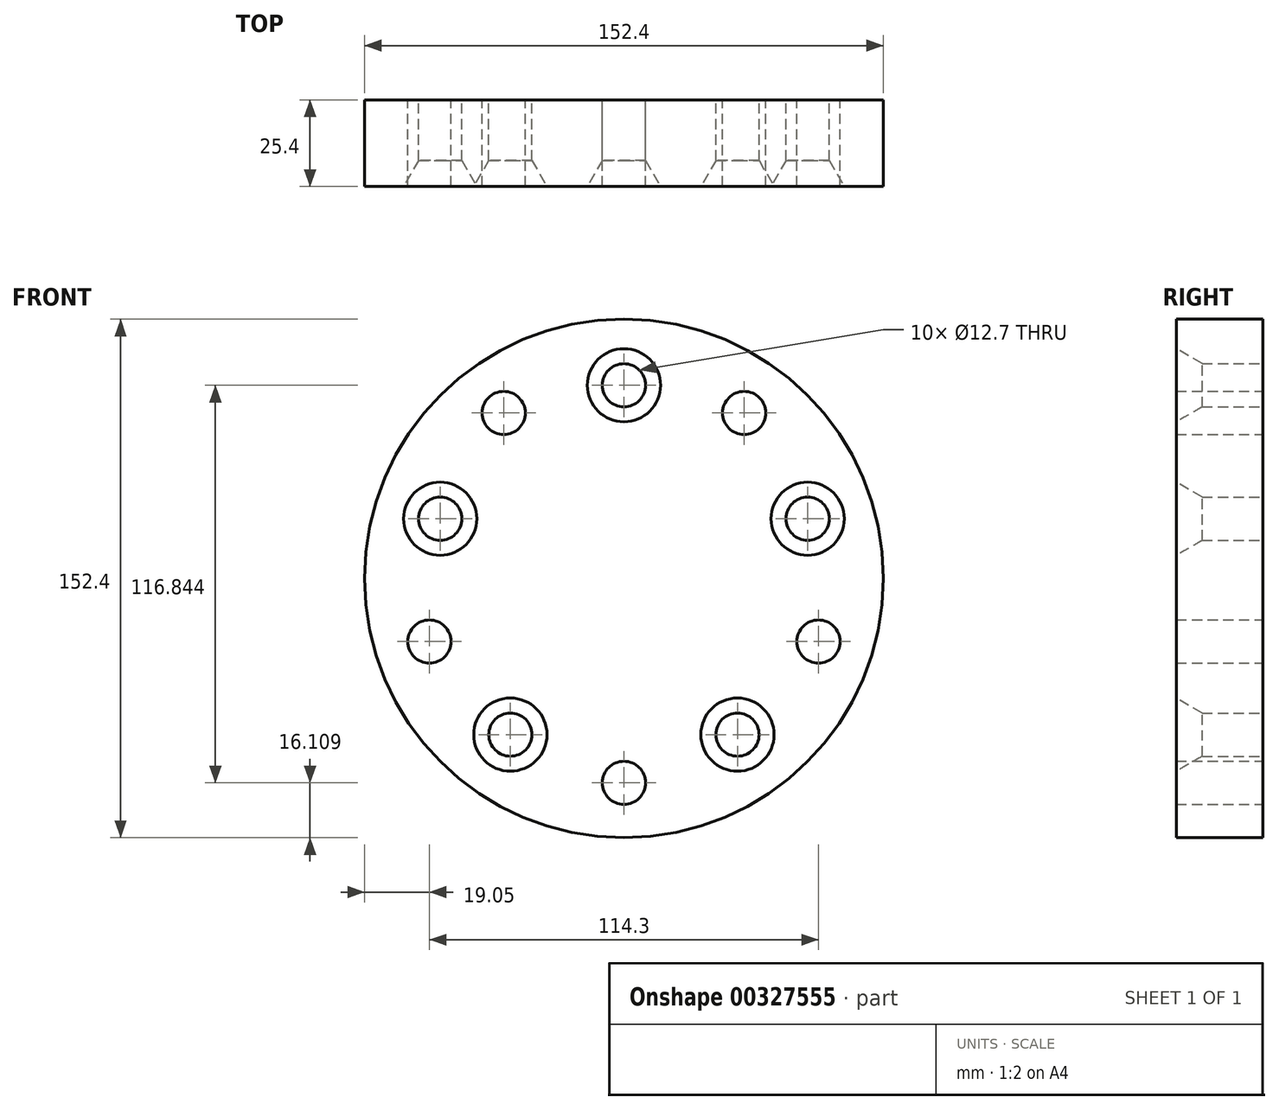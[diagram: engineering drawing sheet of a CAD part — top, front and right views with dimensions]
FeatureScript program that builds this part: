
annotation { "Feature Type Name" : "Feature", "Feature Type Description" : "" }
export const myFeature = defineFeature(function(context is Context, id is Id, definition is map)
    precondition{}
    {
        {
            var Q0;
            Q0=qCreatedBy(makeId("Front.planeOp"),FACE);
            var sketch = newSketch(context, id + "F0", { "sketchPlane" : qUnion([Q0])});
            skCircle(sketch, "E0", {"center": v(0, 0) * mm, "radius": 76.2 * mm});
            skCircle(sketch, "E1", {"center": v(0, 56.75) * mm, "radius": 6.35 * mm});
            skCircle(sketch, "E2.1.0", {"center": v(-53.97, 17.54) * mm, "radius": 6.35 * mm});
            skCircle(sketch, "E2.2.0", {"center": v(-33.36, -45.91) * mm, "radius": 6.35 * mm});
            skCircle(sketch, "E2.3.0", {"center": v(33.36, -45.91) * mm, "radius": 6.35 * mm});
            skCircle(sketch, "E2.4.0", {"center": v(53.98, 17.54) * mm, "radius": 6.35 * mm});
            skCircle(sketch, "E3", {"center": v(0, -60.1) * mm, "radius": 6.35 * mm});
            skCircle(sketch, "E4.1.0", {"center": v(57.15, -18.57) * mm, "radius": 6.35 * mm});
            skCircle(sketch, "E4.2.0", {"center": v(35.32, 48.61) * mm, "radius": 6.35 * mm});
            skCircle(sketch, "E4.3.0", {"center": v(-35.32, 48.61) * mm, "radius": 6.35 * mm});
            skCircle(sketch, "E4.4.0", {"center": v(-57.15, -18.57) * mm, "radius": 6.35 * mm});
            skSolve(sketch);
        }
        {
            var Q0;
            Q0 = qSketchRegion(id + "F0", true);
            extrude(context, id + "F1", {"entities" : qUnion([Q0]), "depth" : 25.4 * mm});
        }
        {
            var Q0;
            Q0=makeQuery(id+"F1.opExtrude","CAP_EDGE",EDGE,{"disambiguationData":[OSD([sQuery(id+"F0.wireOp",EDGE,"E1")])],"isStart":false});
            var Q1;
            Q1=makeQuery(id+"F1.opExtrude","CAP_EDGE",EDGE,{"disambiguationData":[OSD([sQuery(id+"F0.wireOp",EDGE,"E2.4.0")])],"isStart":false});
            var Q2;
            Q2=makeQuery(id+"F1.opExtrude","CAP_EDGE",EDGE,{"disambiguationData":[OSD([sQuery(id+"F0.wireOp",EDGE,"E2.3.0")])],"isStart":false});
            var Q3;
            Q3=makeQuery(id+"F1.opExtrude","CAP_EDGE",EDGE,{"disambiguationData":[OSD([sQuery(id+"F0.wireOp",EDGE,"E2.2.0")])],"isStart":false});
            var Q4;
            Q4=makeQuery(id+"F1.opExtrude","CAP_EDGE",EDGE,{"disambiguationData":[OSD([sQuery(id+"F0.wireOp",EDGE,"E2.1.0")])],"isStart":false});
            chamfer(context, id + "F2", {"entities" : qUnion([Q0, Q1, Q2, Q3, Q4]), "chamferType" : ChamferType.OFFSET_ANGLE, "width" : 7.62 * mm, "oppositeDirection" : false, "angle" : 30 * degree, "tangentPropagation" : true});
        }
    });
